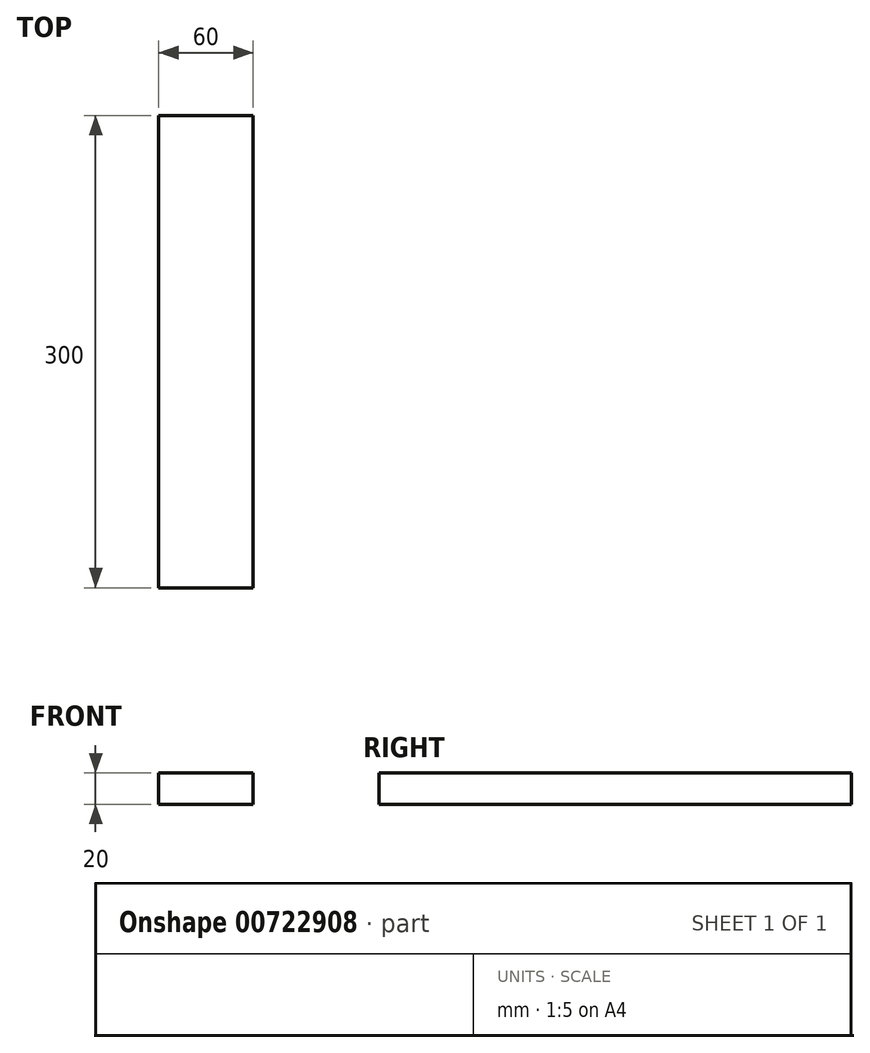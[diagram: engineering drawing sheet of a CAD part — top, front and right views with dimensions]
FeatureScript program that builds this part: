
annotation { "Feature Type Name" : "Feature", "Feature Type Description" : "" }
export const myFeature = defineFeature(function(context is Context, id is Id, definition is map)
    precondition{}
    {
        {
            var Q0;
            Q0=qCreatedBy(makeId("Top.planeOp"),FACE);
            var sketch = newSketch(context, id + "F0", { "sketchPlane" : qUnion([Q0])});
            skLineSegment(sketch, "E0.bottom", {"start": v(30, 150) * mm, "end": v(-30, 150) * mm});
            skLineSegment(sketch, "E0.top", {"start": v(30, -150) * mm, "end": v(-30, -150) * mm});
            skLineSegment(sketch, "E0.left", {"start": v(30, 150) * mm, "end": v(30, -150) * mm});
            skLineSegment(sketch, "E0.right", {"start": v(-30, 150) * mm, "end": v(-30, -150) * mm});
            skPoint(sketch, "E0.middle", {"position": v(0, 0) * mm});
            skSolve(sketch);
        }
        {
            var Q0;
            Q0=makeQuery(id+"F0.imprint","IMPRINT",FACE,{"disambiguationData":[TD([[makeQuery(id+"F0.imprint","IMPRINT",EDGE,{"derivedFrom":sQuery(id+"F0.wireOp",EDGE,"E0.bottom")}),1.0]])]});
            extrude(context, id + "F1", {"entities" : qUnion([Q0]), "depth" : 20 * mm, "offsetDistance" : 25 * mm});
        }
    });
